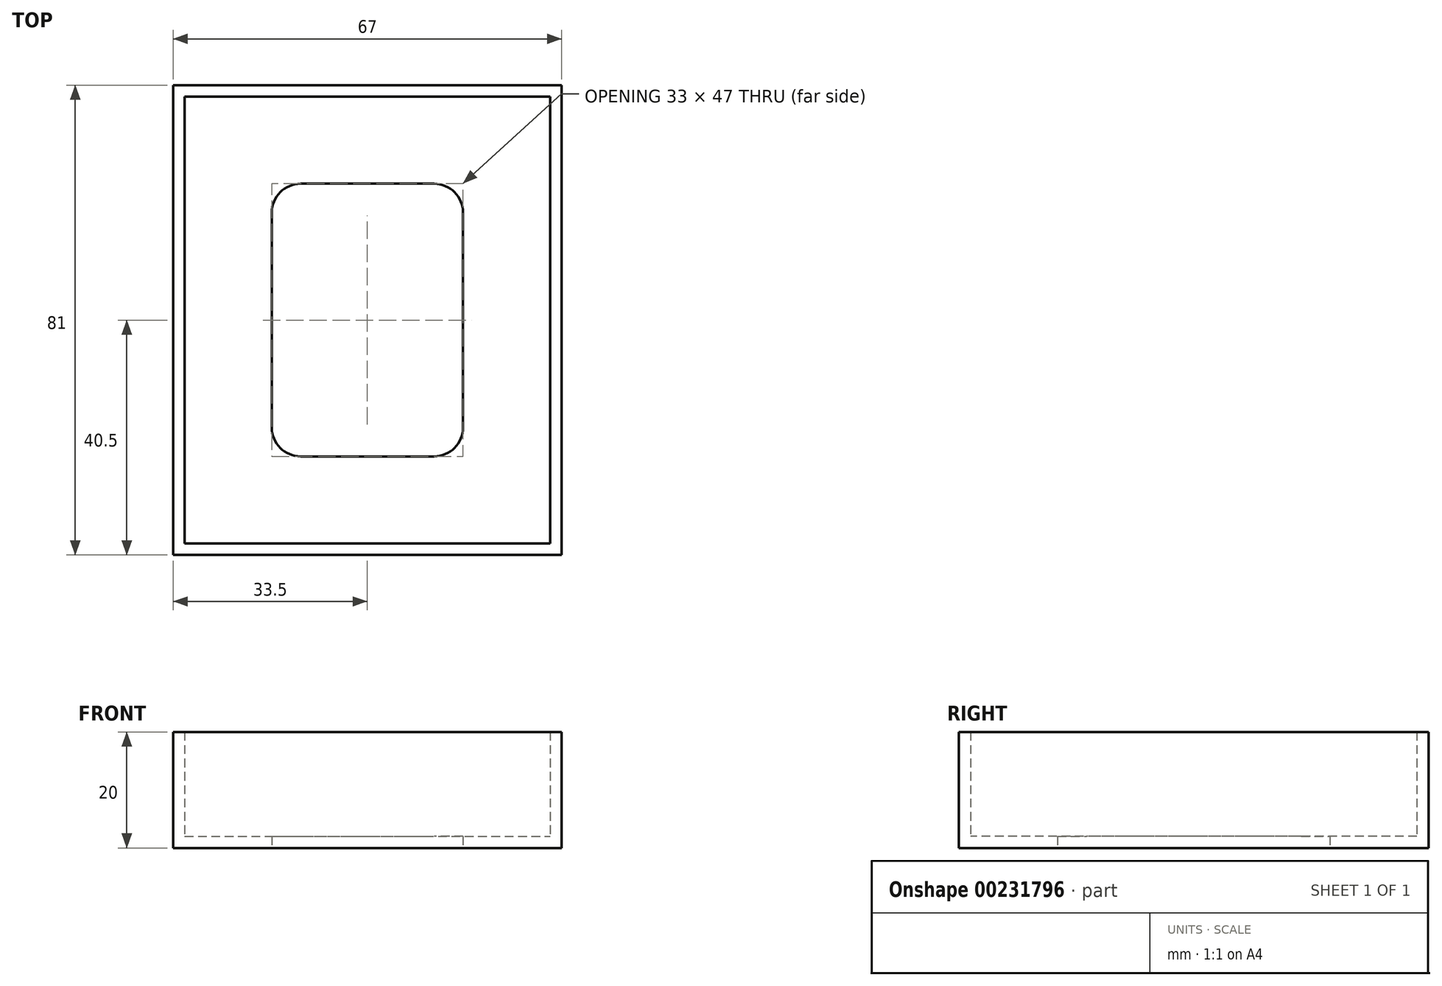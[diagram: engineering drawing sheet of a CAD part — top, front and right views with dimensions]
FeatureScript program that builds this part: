
annotation { "Feature Type Name" : "Feature", "Feature Type Description" : "" }
export const myFeature = defineFeature(function(context is Context, id is Id, definition is map)
    precondition{}
    {
        {
            var Q0;
            Q0=qCreatedBy(makeId("Top.planeOp"),FACE);
            var sketch = newSketch(context, id + "F0", { "sketchPlane" : qUnion([Q0])});
            skLineSegment(sketch, "E0.bottom", {"start": v(-31.5, 38.5) * mm, "end": v(31.5, 38.5) * mm});
            skLineSegment(sketch, "E0.top", {"start": v(-31.5, -38.5) * mm, "end": v(31.5, -38.5) * mm});
            skLineSegment(sketch, "E0.left", {"start": v(-31.5, 38.5) * mm, "end": v(-31.5, -38.5) * mm});
            skLineSegment(sketch, "E0.right", {"start": v(31.5, 38.5) * mm, "end": v(31.5, -38.5) * mm});
            skLineSegment(sketch, "E1.bottom", {"start": v(-33.5, 40.5) * mm, "end": v(33.5, 40.5) * mm});
            skLineSegment(sketch, "E1.top", {"start": v(-33.5, -40.5) * mm, "end": v(33.5, -40.5) * mm});
            skLineSegment(sketch, "E1.left", {"start": v(-33.5, 40.5) * mm, "end": v(-33.5, -40.5) * mm});
            skLineSegment(sketch, "E1.right", {"start": v(33.5, 40.5) * mm, "end": v(33.5, -40.5) * mm});
            skLineSegment(sketch, "E2.bottom", {"start": v(-11.5, 23.5) * mm, "end": v(11.5, 23.5) * mm});
            skLineSegment(sketch, "E2.top", {"start": v(-11.5, -23.5) * mm, "end": v(11.5, -23.5) * mm});
            skLineSegment(sketch, "E2.left", {"start": v(-16.5, 18.5) * mm, "end": v(-16.5, -18.5) * mm});
            skLineSegment(sketch, "E2.right", {"start": v(16.5, 18.5) * mm, "end": v(16.5, -18.5) * mm});
            skPoint(sketch, "E3.visualSharp", {"position": v(-16.5, 23.5) * mm});
            skArc(sketch, "E3.filletArc", {"start": v(-11.5, 23.5) * mm, "mid": v(-15.04, 22.04) * mm, "end": v(-16.5, 18.5) * mm});
            skPoint(sketch, "E4.visualSharp", {"position": v(16.5, 23.5) * mm});
            skArc(sketch, "E4.filletArc", {"start": v(16.5, 18.5) * mm, "mid": v(15.04, 22.04) * mm, "end": v(11.5, 23.5) * mm});
            skPoint(sketch, "E5.visualSharp", {"position": v(16.5, -23.5) * mm});
            skArc(sketch, "E5.filletArc", {"start": v(11.5, -23.5) * mm, "mid": v(15.04, -22.04) * mm, "end": v(16.5, -18.5) * mm});
            skPoint(sketch, "E6.visualSharp", {"position": v(-16.5, -23.5) * mm});
            skArc(sketch, "E6.filletArc", {"start": v(-16.5, -18.5) * mm, "mid": v(-15.04, -22.04) * mm, "end": v(-11.5, -23.5) * mm});
            skSolve(sketch);
        }
        {
            var Q0;
            Q0=makeQuery(id+"F0.imprint","IMPRINT",FACE,{"disambiguationData":[TD([[makeQuery(id+"F0.imprint","IMPRINT",EDGE,{"derivedFrom":sQuery(id+"F0.wireOp",EDGE,"E0.bottom")}),-1.0]])]});
            extrude(context, id + "F1", {"entities" : qUnion([Q0]), "depth" : 2 * mm});
        }
        {
            var Q0;
            Q0=makeQuery(id+"F0.imprint","IMPRINT",FACE,{"disambiguationData":[TD([[makeQuery(id+"F0.imprint","IMPRINT",EDGE,{"derivedFrom":sQuery(id+"F0.wireOp",EDGE,"E0.bottom")}),1.0]])]});
            extrude(context, id + "F2", {"entities" : qUnion([Q0]), "operationType" : NewBodyOperationType.ADD, "depth" : 20 * mm});
        }
    });
